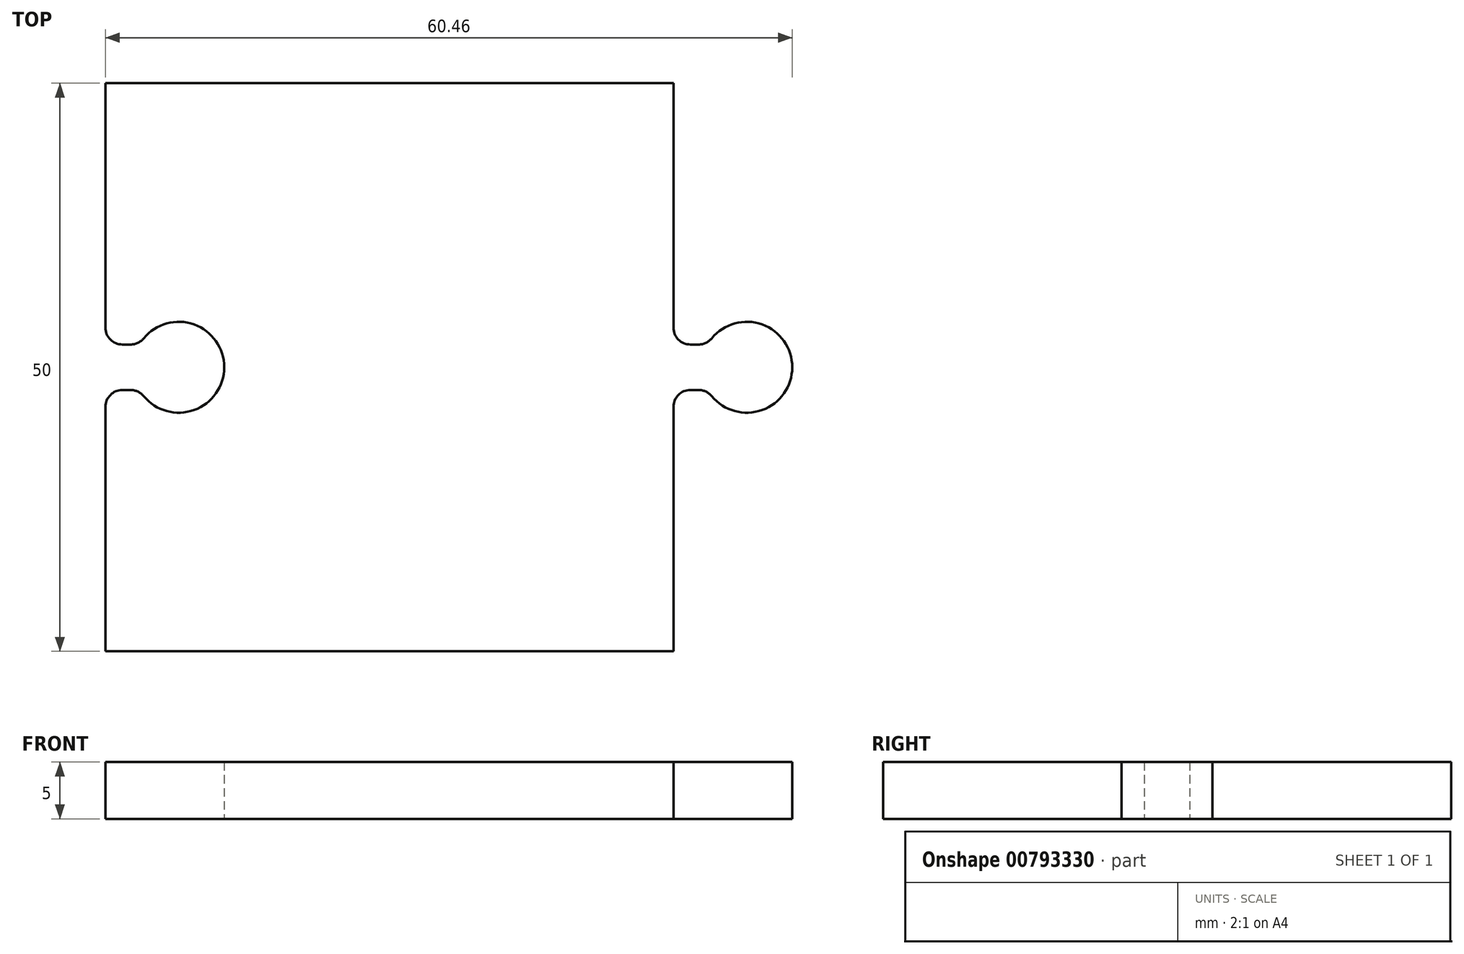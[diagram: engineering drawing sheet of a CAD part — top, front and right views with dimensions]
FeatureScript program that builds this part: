
annotation { "Feature Type Name" : "Feature", "Feature Type Description" : "" }
export const myFeature = defineFeature(function(context is Context, id is Id, definition is map)
    precondition{}
    {
        {
            var Q0;
            Q0=qCreatedBy(makeId("Top.planeOp"),FACE);
            var sketch = newSketch(context, id + "F0", { "sketchPlane" : qUnion([Q0])});
            skLineSegment(sketch, "E0.bottom", {"start": v(-28.3, 29.8) * mm, "end": v(21.7, 29.8) * mm});
            skLineSegment(sketch, "E0.top", {"start": v(-28.3, -20.2) * mm, "end": v(21.7, -20.2) * mm});
            skLineSegment(sketch, "E0.left", {"start": v(-28.3, 29.8) * mm, "end": v(-28.3, 8.3) * mm});
            skLineSegment(sketch, "E0.right", {"start": v(21.7, 1.3) * mm, "end": v(21.7, -20.2) * mm});
            skLineSegment(sketch, "E1", {"start": v(23.2, 6.8) * mm, "end": v(23.92, 6.8) * mm});
            skLineSegment(sketch, "E2", {"start": v(32.16, 4.8) * mm, "end": v(32.16, 2.8) * mm});
            skPoint(sketch, "E3.newPointB", {"position": v(21.7, 29.8) * mm});
            skArc(sketch, "E3.filletArc", {"start": v(23.2, 2.8) * mm, "mid": v(22.14, 2.36) * mm, "end": v(21.7, 1.3) * mm});
            skLineSegment(sketch, "E4", {"start": v(21.7, 29.8) * mm, "end": v(21.7, 8.3) * mm});
            skPoint(sketch, "E5.visualSharp", {"position": v(21.7, 6.8) * mm});
            skArc(sketch, "E5.filletArc", {"start": v(21.7, 8.3) * mm, "mid": v(22.14, 7.24) * mm, "end": v(23.2, 6.8) * mm});
            skArc(sketch, "E6", {"start": v(25.08, 2.25) * mm, "mid": v(32.16, 4.8) * mm, "end": v(25.08, 7.34) * mm});
            skPoint(sketch, "E6.centerSnap0", {"position": v(32.16, 4.8) * mm});
            skPoint(sketch, "E7.orphan", {"position": v(32.16, 6.8) * mm});
            skLineSegment(sketch, "E8.trimOffspring", {"start": v(23.92, 2.8) * mm, "end": v(23.2, 2.8) * mm});
            skPoint(sketch, "E9.end.orphan", {"position": v(21.7, 2.8) * mm});
            skArc(sketch, "E10", {"start": v(-24.92, 2.25) * mm, "mid": v(-17.84, 4.8) * mm, "end": v(-24.92, 7.34) * mm});
            skLineSegment(sketch, "E11", {"start": v(-26.8, 6.8) * mm, "end": v(-26.08, 6.8) * mm});
            skLineSegment(sketch, "E12", {"start": v(-26.8, 2.8) * mm, "end": v(-26.08, 2.8) * mm});
            skLineSegment(sketch, "E13.trimOffspring", {"start": v(-28.3, 1.3) * mm, "end": v(-28.3, -20.2) * mm});
            skPoint(sketch, "E14.orphan", {"position": v(-28.3, 4.8) * mm});
            skPoint(sketch, "E15.end.orphan", {"position": v(-17.84, 4.8) * mm});
            skPoint(sketch, "E16.visualSharp", {"position": v(-28.3, 6.8) * mm});
            skArc(sketch, "E16.filletArc", {"start": v(-28.3, 8.3) * mm, "mid": v(-27.86, 7.24) * mm, "end": v(-26.8, 6.8) * mm});
            skPoint(sketch, "E17.visualSharp", {"position": v(-28.3, 2.8) * mm});
            skArc(sketch, "E17.filletArc", {"start": v(-26.8, 2.8) * mm, "mid": v(-27.86, 2.36) * mm, "end": v(-28.3, 1.3) * mm});
            skPoint(sketch, "E18.visualSharp", {"position": v(-25.3, 6.8) * mm});
            skArc(sketch, "E18.filletArc", {"start": v(-26.08, 6.8) * mm, "mid": v(-25.44, 6.94) * mm, "end": v(-24.92, 7.34) * mm});
            skPoint(sketch, "E19.visualSharp", {"position": v(-25.3, 2.8) * mm});
            skArc(sketch, "E19.filletArc", {"start": v(-24.92, 2.25) * mm, "mid": v(-25.44, 2.65) * mm, "end": v(-26.08, 2.8) * mm});
            skPoint(sketch, "E20.visualSharp", {"position": v(24.7, 2.8) * mm});
            skArc(sketch, "E20.filletArc", {"start": v(25.08, 2.25) * mm, "mid": v(24.56, 2.65) * mm, "end": v(23.92, 2.8) * mm});
            skPoint(sketch, "E21.visualSharp", {"position": v(24.7, 6.8) * mm});
            skArc(sketch, "E21.filletArc", {"start": v(23.92, 6.8) * mm, "mid": v(24.56, 6.94) * mm, "end": v(25.08, 7.34) * mm});
            skPoint(sketch, "E22.start.orphan", {"position": v(21.7, 4.8) * mm});
            skSolve(sketch);
        }
        {
            var Q0;
            Q0 = qSketchRegion(id + "F0", true);
            extrude(context, id + "F1", {"entities" : qUnion([Q0]), "depth" : 5 * mm, "offsetDistance" : 25 * mm});
        }
    });
